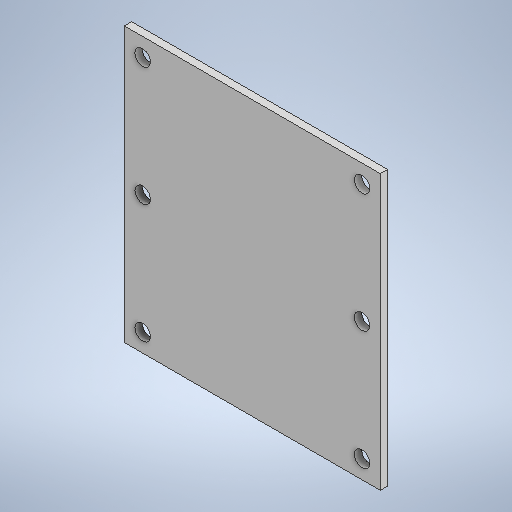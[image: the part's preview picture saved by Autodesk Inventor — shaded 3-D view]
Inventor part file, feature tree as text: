
AUTODESK INVENTOR PART (.ipt)
format: ipt  version: 2025 (Build 290162010, 162A)  size: 242,176 bytes
history: native  units: mm
features: sketch x2, sheet_metal_op x1, hole x1, mirror x1, other x1, projected_geometry x1
ambient origin geometry x8: Origin, YZ Plane, XZ Plane, XY Plane, X Axis, Y Axis, Z Axis, Center Point
bodies: Solid1 (feature_tree)
feature tree (7):
  sheet_metal_op  "Face1"
  hole  "Hole1"  [1 undecoded]
  mirror  "Mirror1"
  sketch  "Sketch1"  dims[d2=8.0mm]
  other  "Plate1"
  sketch  "Sketch2"  dims[d3=17.0mm d4=6.0mm d5=4.0mm d6=2.0mm d7=90.0deg d8=8.0mm d9=20.594885mm d16=280.0mm d17=300.0mm d19=20.0mm d20=20.0mm]
  projected_geometry  "Projected Loop1"
note: 1 required parameter value undecoded (feature->parameter linkage not recoverable at this tier; creation-order binding heuristic only, values carry confidence <= 0.55)
